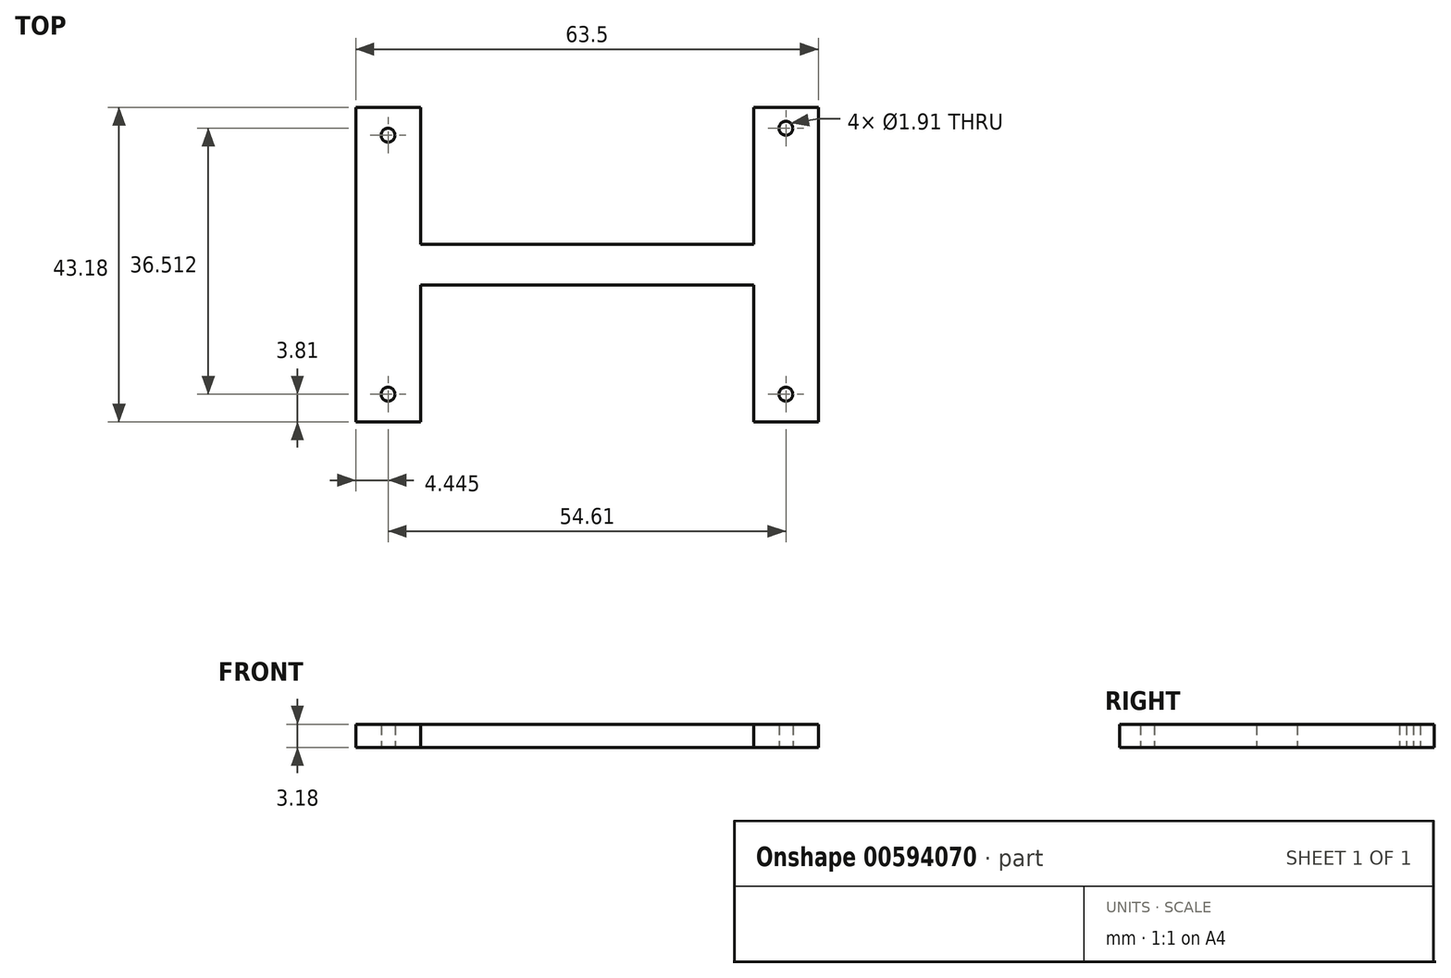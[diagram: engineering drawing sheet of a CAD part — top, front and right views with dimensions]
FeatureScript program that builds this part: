
annotation { "Feature Type Name" : "Feature", "Feature Type Description" : "" }
export const myFeature = defineFeature(function(context is Context, id is Id, definition is map)
    precondition{}
    {
        {
            var Q0;
            Q0=qCreatedBy(makeId("Top.planeOp"),FACE);
            var sketch = newSketch(context, id + "F0", { "sketchPlane" : qUnion([Q0])});
            skLineSegment(sketch, "E0", {"start": v(0, 0) * mm, "end": v(0, -43.18) * mm});
            skLineSegment(sketch, "E1", {"start": v(0, -43.18) * mm, "end": v(8.89, -43.18) * mm});
            skLineSegment(sketch, "E2", {"start": v(0, 0) * mm, "end": v(8.9, 0) * mm});
            skLineSegment(sketch, "E3", {"start": v(8.9, 0) * mm, "end": v(8.9, -18.8) * mm});
            skLineSegment(sketch, "E4", {"start": v(8.9, -43.18) * mm, "end": v(8.9, -24.38) * mm});
            skLineSegment(sketch, "E5.MirrorCS", {"start": v(54.6, 0) * mm, "end": v(54.6, -18.8) * mm});
            skLineSegment(sketch, "E6.MirrorCS", {"start": v(63.5, 0) * mm, "end": v(63.5, -43.18) * mm});
            skLineSegment(sketch, "E7.MirrorCS", {"start": v(54.6, -43.18) * mm, "end": v(54.6, -24.38) * mm});
            skLineSegment(sketch, "E8", {"start": v(8.89, -18.8) * mm, "end": v(54.61, -18.8) * mm});
            skLineSegment(sketch, "E9", {"start": v(54.61, -24.38) * mm, "end": v(8.89, -24.38) * mm});
            skLineSegment(sketch, "E10.trimOffspring", {"start": v(54.6, 0) * mm, "end": v(63.5, 0) * mm});
            skLineSegment(sketch, "E11", {"start": v(54.61, -43.18) * mm, "end": v(63.5, -43.18) * mm});
            skCircle(sketch, "E12", {"center": v(4.44, -3.81) * mm, "radius": 0.95 * mm});
            skLineSegment(sketch, "E13", {"start": v(4.45, 0) * mm, "end": v(4.45, -3.81) * mm, "construction": true});
            skLineSegment(sketch, "E14", {"start": v(4.44, -3.81) * mm, "end": v(0, -3.81) * mm, "construction": true});
            skLineSegment(sketch, "E15", {"start": v(0, -21.59) * mm, "end": v(4.15, -21.59) * mm, "construction": true});
            skLineSegment(sketch, "E16", {"start": v(31.75, -18.8) * mm, "end": v(31.75, -21.94) * mm, "construction": true});
            skCircle(sketch, "E17", {"center": v(4.44, -39.37) * mm, "radius": 0.95 * mm});
            skLineSegment(sketch, "E18", {"start": v(4.44, -43.18) * mm, "end": v(4.44, -39.37) * mm, "construction": true});
            skLineSegment(sketch, "E19", {"start": v(4.44, -39.37) * mm, "end": v(0, -39.37) * mm, "construction": true});
            skCircle(sketch, "E20", {"center": v(59.06, -2.86) * mm, "radius": 0.95 * mm});
            skLineSegment(sketch, "E21", {"start": v(59.06, 0) * mm, "end": v(59.06, -2.86) * mm, "construction": true});
            skCircle(sketch, "E22", {"center": v(59.06, -39.37) * mm, "radius": 0.95 * mm});
            skLineSegment(sketch, "E23", {"start": v(59.06, -39.37) * mm, "end": v(59.06, -43.18) * mm, "construction": true});
            skSolve(sketch);
        }
        {
            var Q0;
            Q0=makeQuery(id+"F0.imprint","IMPRINT",FACE,{"disambiguationData":[TD([[makeQuery(id+"F0.imprint","IMPRINT",EDGE,{"derivedFrom":sQuery(id+"F0.wireOp",EDGE,"E0")}),1.0]])]});
            extrude(context, id + "F1", {"entities" : qUnion([Q0]), "depth" : 3.17 * mm, "offsetDistance" : 25.4 * mm});
        }
    });
